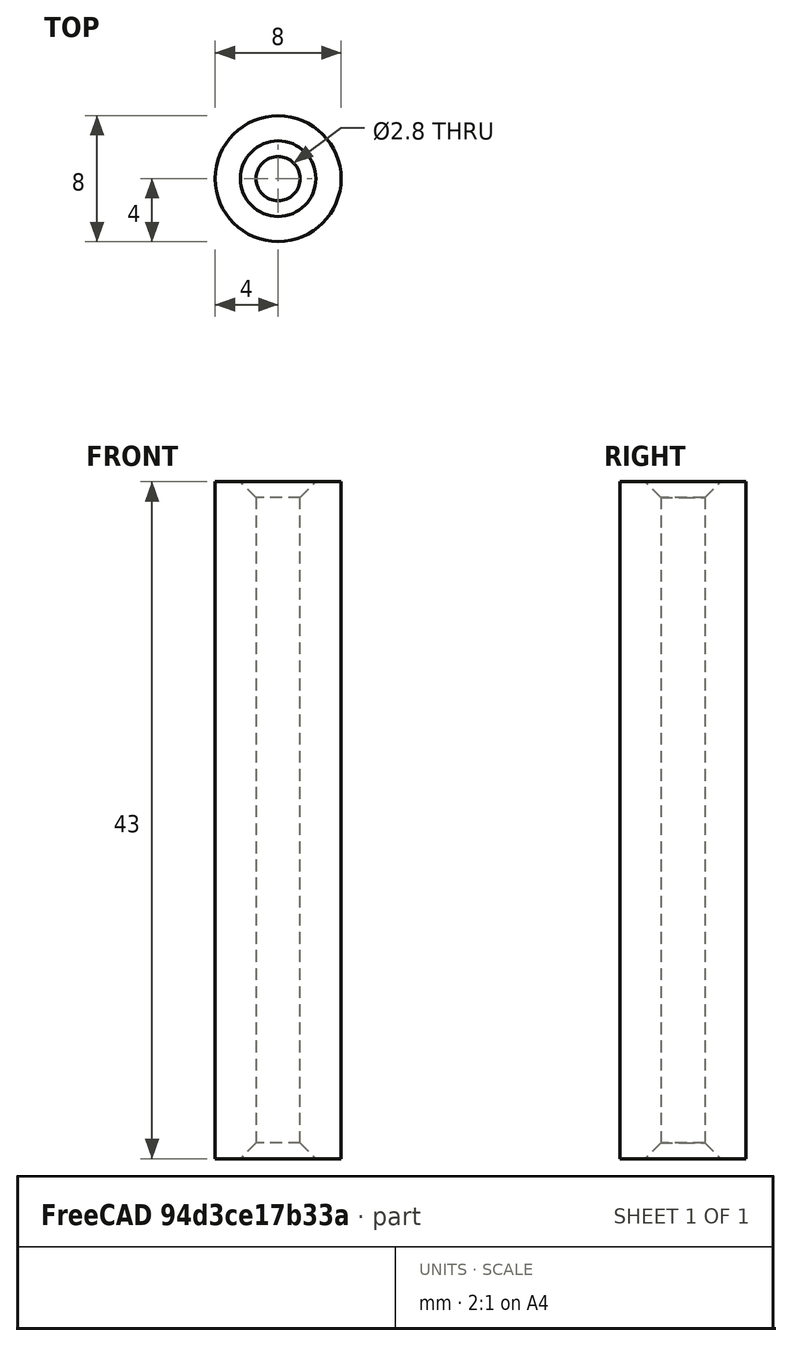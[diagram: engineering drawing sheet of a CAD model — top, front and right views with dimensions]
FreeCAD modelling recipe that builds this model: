
FCSTD DOCUMENT  (FreeCAD 1.0R39109 (Git))
Label: 2_8x8x43mm_spacer
License: All rights reserved
LicenseURL: https://en.wikipedia.org/wiki/All_rights_reserved
objects: Sketcher::SketchObject×1, PartDesign::Pad×1, PartDesign::Chamfer×1, PartDesign::Body×1
note: 9 computed .brp shape members not serialized (recipe doc carries the construction recipe); baked Part::Feature solids carry a one-line shape summary decoded from their .brp

FEATURE [Sketcher::SketchObject] Sketch
  ArcFitTolerance = 1e-06
  AttachmentSupport = -> [XY_Plane]
  FullyConstrained = true
  MakeInternals = false
  MapMode = 5
  sketch-geometry (2):
    g0: Circle CenterX=0 CenterY=0 CenterZ=0 NormalX=0 NormalY=0 NormalZ=1 AngleXU=0 Radius=1.4
    g1: Circle CenterX=0 CenterY=0 CenterZ=0 NormalX=0 NormalY=0 NormalZ=1 AngleXU=0 Radius=4
  constraints (4):
    c: Coincident(g0,g-1)
    c: Coincident(g1,g0)
    c: Diameter(g0) = 2.8
    c: Diameter(g1) = 8
FEATURE [PartDesign::Pad] Pad
  Direction = (0,0,1)
  Length = 43
  Length2 = 10
  Profile = -> Sketch
  ReferenceAxis = -> Sketch [N_Axis]
  Refine = true
  Suppressed = false
  Type = 0
FEATURE [PartDesign::Chamfer] Chamfer
  Angle = 45
  Base = -> Pad [Edge6,Edge5]
  BaseFeature = -> Pad
  ChamferType = 0
  FlipDirection = false
  Refine = true
  Size = 1
  Size2 = 1
  SupportTransform = false
  Suppressed = false
  UseAllEdges = false
FEATURE [PartDesign::Body] Body
  AllowCompound = false
  Group = -> [Sketch,Pad,Chamfer]
  Origin = -> Origin
  Tip = -> Chamfer
